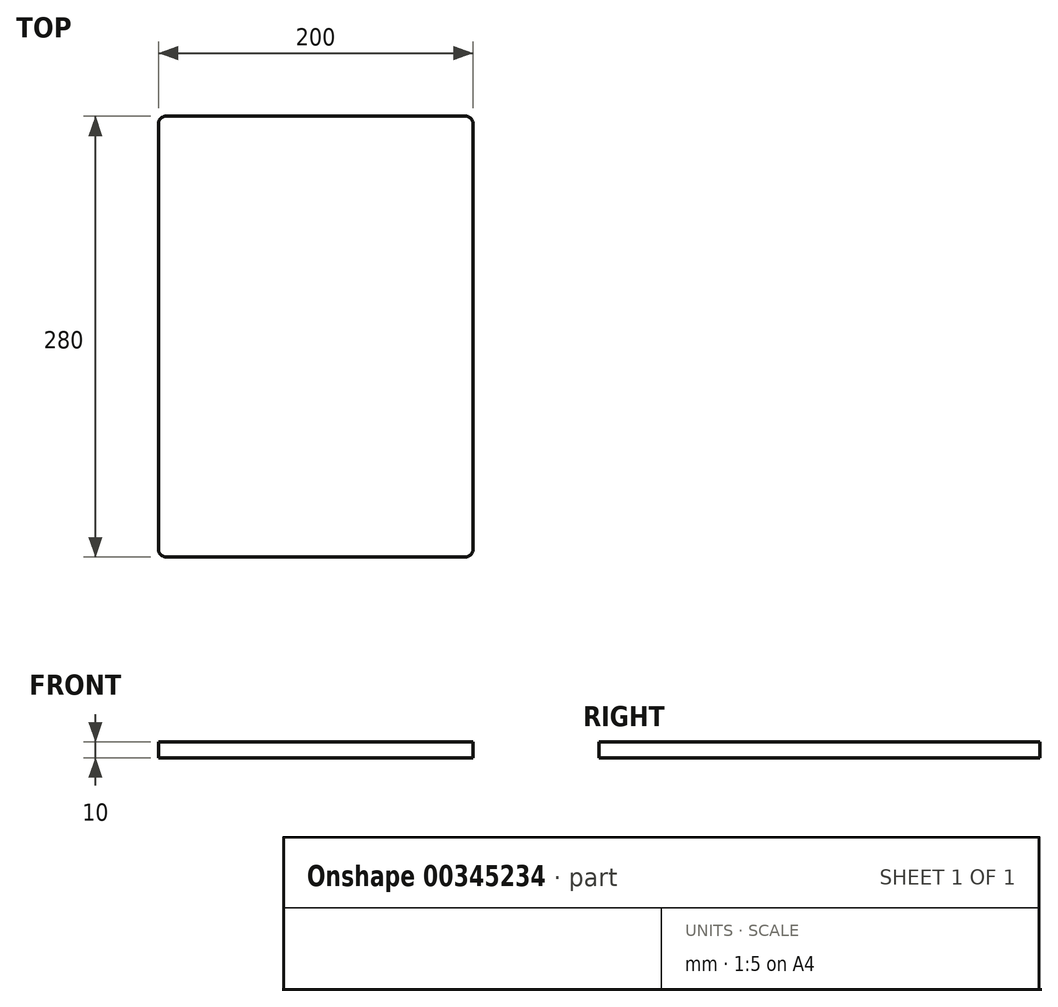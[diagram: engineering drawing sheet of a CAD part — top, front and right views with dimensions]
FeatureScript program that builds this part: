
annotation { "Feature Type Name" : "Feature", "Feature Type Description" : "" }
export const myFeature = defineFeature(function(context is Context, id is Id, definition is map)
    precondition{}
    {
        {
            var Q0;
            Q0=qCreatedBy(makeId("Top.planeOp"),FACE);
            var sketch = newSketch(context, id + "F0", { "sketchPlane" : qUnion([Q0])});
            skLineSegment(sketch, "E0.bottom", {"start": v(-95, 140) * mm, "end": v(95, 140) * mm});
            skLineSegment(sketch, "E0.top", {"start": v(-95, -140) * mm, "end": v(95, -140) * mm});
            skLineSegment(sketch, "E0.left", {"start": v(-100, 135) * mm, "end": v(-100, -135) * mm});
            skLineSegment(sketch, "E0.right", {"start": v(100, 135) * mm, "end": v(100, -135) * mm});
            skPoint(sketch, "E0.middle", {"position": v(0, 0) * mm});
            skPoint(sketch, "E1.visualSharp", {"position": v(-100, 140) * mm});
            skArc(sketch, "E1.filletArc", {"start": v(-95, 140) * mm, "mid": v(-98.54, 138.54) * mm, "end": v(-100, 135) * mm});
            skPoint(sketch, "E2.visualSharp", {"position": v(100, 140) * mm});
            skArc(sketch, "E2.filletArc", {"start": v(100, 135) * mm, "mid": v(98.54, 138.54) * mm, "end": v(95, 140) * mm});
            skPoint(sketch, "E3.visualSharp", {"position": v(100, -140) * mm});
            skArc(sketch, "E3.filletArc", {"start": v(95, -140) * mm, "mid": v(98.54, -138.54) * mm, "end": v(100, -135) * mm});
            skPoint(sketch, "E4.visualSharp", {"position": v(-100, -140) * mm});
            skArc(sketch, "E4.filletArc", {"start": v(-100, -135) * mm, "mid": v(-98.54, -138.54) * mm, "end": v(-95, -140) * mm});
            skSolve(sketch);
        }
        {
            var Q0;
            Q0=qSketchRegion(id+"F0",true);
            extrude(context, id + "F1", {"entities" : qUnion([Q0]), "depth" : 10 * mm});
        }
    });
